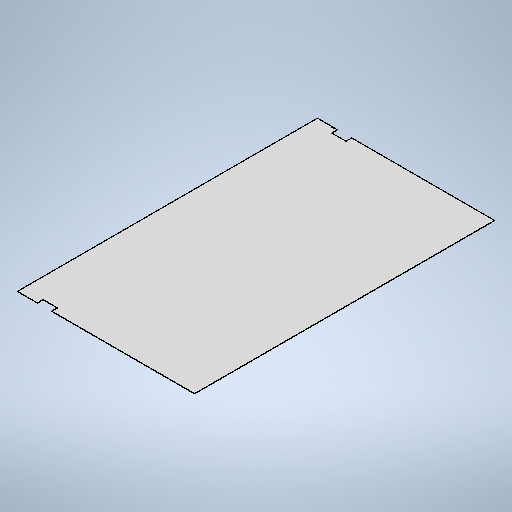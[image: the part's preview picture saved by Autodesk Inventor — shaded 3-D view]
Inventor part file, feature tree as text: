
AUTODESK INVENTOR PART (.ipt)
format: ipt  version: 2025.3 (Build 293356000, 356)  size: 304,128 bytes
history: native  units: mm
features: other x3, sketch x2, sheet_metal_op x1
ambient origin geometry x8: Origin, YZ Plane, XZ Plane, XY Plane, X Axis, Y Axis, Z Axis, Center Point
bodies: Solid1 (feature_tree)
feature tree (6):
  sheet_metal_op  "Face1"
  sketch  "Sketch1"  dims[d2=3.0mm]
  other  "Plate1"
  sketch  "Sketch6"  dims[d22=1240.0mm d23=2100.0mm d24=40.0mm d25=40.0mm d28=100.0mm d29=960.0mm d38=2.0mm d39=5.0mm d40=0.5mm d41=3.0mm d42=2.0mm d43=5.0mm d44=3.0mm d45=5.0mm d46=100.0mm d47=3.0mm d48=0.0mm]
  other  "Cut1"
  other  "Definition1"
